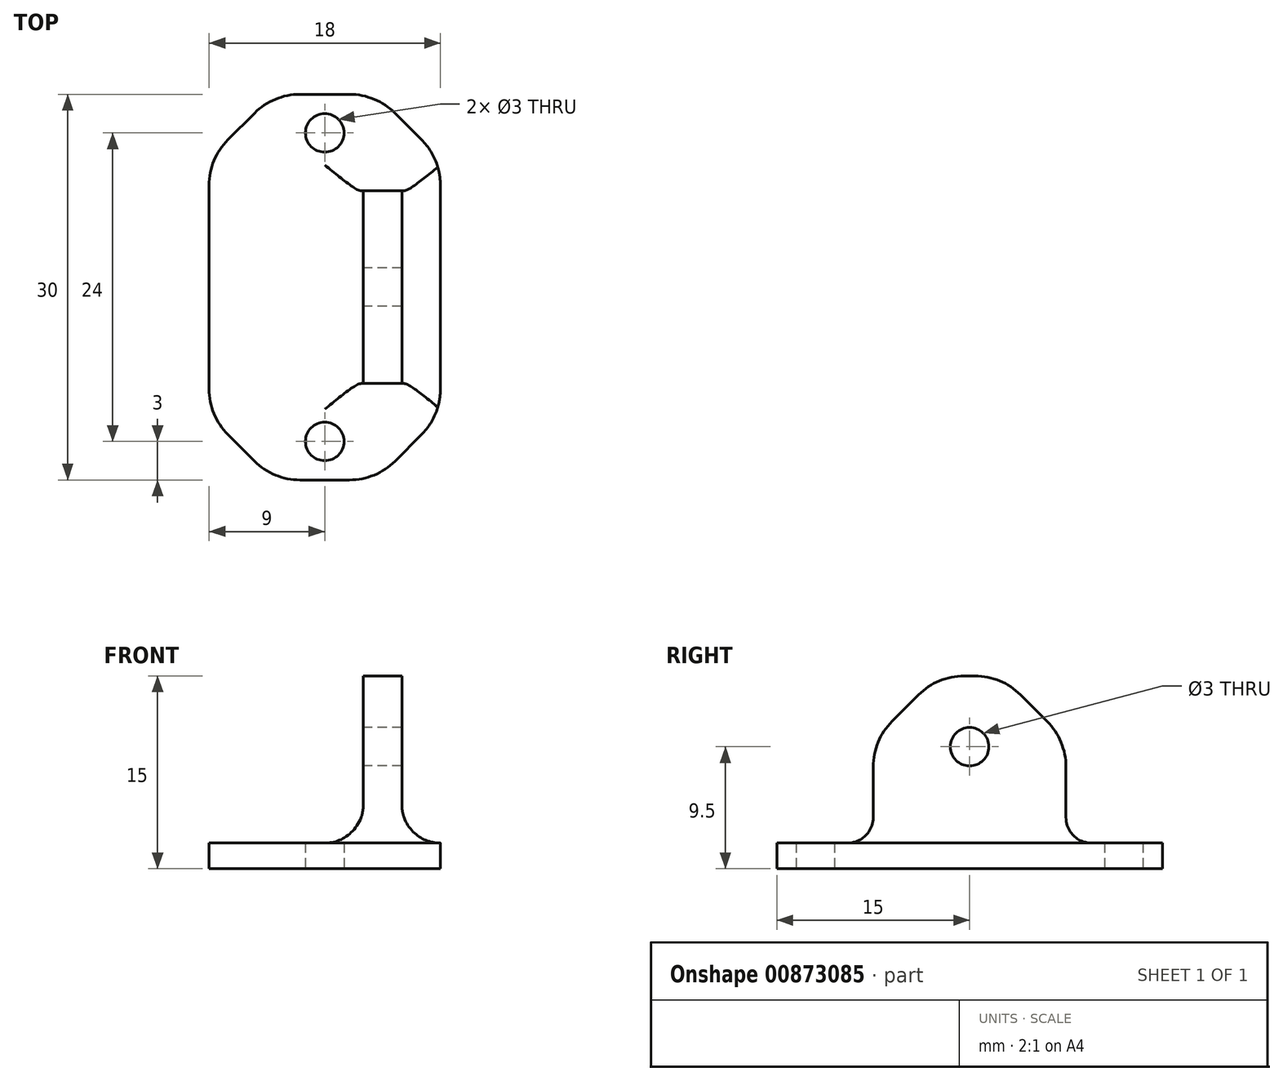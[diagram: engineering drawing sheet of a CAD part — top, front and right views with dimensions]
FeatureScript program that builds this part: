
annotation { "Feature Type Name" : "Feature", "Feature Type Description" : "" }
export const myFeature = defineFeature(function(context is Context, id is Id, definition is map)
    precondition{}
    {
        {
            var Q0;
            Q0=qCreatedBy(makeId("Top.planeOp"),FACE);
            var sketch = newSketch(context, id + "F0", { "sketchPlane" : qUnion([Q0])});
            skLineSegment(sketch, "E0.bottom", {"start": v(9, -15) * mm, "end": v(-9, -15) * mm});
            skLineSegment(sketch, "E0.top", {"start": v(9, 15) * mm, "end": v(-9, 15) * mm});
            skLineSegment(sketch, "E0.left", {"start": v(9, -15) * mm, "end": v(9, 15) * mm});
            skLineSegment(sketch, "E0.right", {"start": v(-9, -15) * mm, "end": v(-9, 15) * mm});
            skPoint(sketch, "E0.middle", {"position": v(0, 0) * mm});
            skLineSegment(sketch, "E1.bottom", {"start": v(6, -7.5) * mm, "end": v(3, -7.5) * mm});
            skLineSegment(sketch, "E1.top", {"start": v(6, 7.5) * mm, "end": v(3, 7.5) * mm});
            skLineSegment(sketch, "E1.left", {"start": v(6, -7.5) * mm, "end": v(6, 7.5) * mm});
            skLineSegment(sketch, "E1.right", {"start": v(3, -7.5) * mm, "end": v(3, 7.5) * mm});
            skPoint(sketch, "E1.middle", {"position": v(4.5, 0) * mm});
            skLineSegment(sketch, "E2", {"start": v(0, 0) * mm, "end": v(3, 0) * mm});
            skLineSegment(sketch, "E3", {"start": v(4.5, -7.5) * mm, "end": v(4.5, -15) * mm, "construction": true});
            skLineSegment(sketch, "E4", {"start": v(0, 0) * mm, "end": v(0, 12) * mm, "construction": true});
            skLineSegment(sketch, "E5", {"start": v(0, 0) * mm, "end": v(0, -12) * mm, "construction": true});
            skCircle(sketch, "E6", {"center": v(0, 12) * mm, "radius": 1.5 * mm});
            skCircle(sketch, "E7", {"center": v(0, -12) * mm, "radius": 1.5 * mm});
            skSolve(sketch);
        }
        {
            var Q0;
            Q0=makeQuery(id+"F0.imprint","IMPRINT",FACE,{"disambiguationData":[TD([[makeQuery(id+"F0.imprint","IMPRINT",EDGE,{"derivedFrom":sQuery(id+"F0.wireOp",EDGE,"E0.bottom")}),-1.0]])]});
            var Q1;
            {var subQ1=sQuery(id+"F0.wireOp",EDGE,"E1.bottom");Q1=makeQuery(id+"F0.imprint","IMPRINT",FACE,{"disambiguationData":[TD([[makeQuery(id+"F0.imprint","IMPRINT",EDGE,{"derivedFrom":subQ1}),-1.0]])]});}
            extrude(context, id + "F1", {"entities" : qUnion([Q0, Q1]), "depth" : 2 * mm, "offsetDistance" : 25 * mm});
        }
        {
            var Q0;
            {var subQ1=sQuery(id+"F0.wireOp",EDGE,"E1.bottom");Q0=makeQuery(id+"F0.imprint","IMPRINT",FACE,{"disambiguationData":[TD([[makeQuery(id+"F0.imprint","IMPRINT",EDGE,{"derivedFrom":subQ1}),-1.0]])]});}
            extrude(context, id + "F2", {"entities" : qUnion([Q0]), "operationType" : NewBodyOperationType.ADD, "depth" : 15 * mm, "offsetDistance" : 25 * mm});
        }
        {
            var Q0;
            Q0=makeQuery(id+"F2.opExtrude","SWEPT_FACE",FACE,{"disambiguationData":[OSD([sQuery(id+"F0.wireOp",EDGE,"E1.right")])]});
            var sketch = newSketch(context, id + "F3", { "sketchPlane" : qUnion([Q0])});
            skCircle(sketch, "E8", {"center": v(0, 9.5) * mm, "radius": 1.5 * mm});
            skPoint(sketch, "E8.centerSnap0", {"position": v(0, 15) * mm});
            skLineSegment(sketch, "E9", {"start": v(0, 15) * mm, "end": v(0, 9.5) * mm, "construction": true});
            skSolve(sketch);
        }
        {
            var Q0;
            Q0=makeQuery(id+"F3.imprint","IMPRINT",FACE,{"disambiguationData":[TD([[makeQuery(id+"F3.imprint","IMPRINT",EDGE,{"derivedFrom":sQuery(id+"F3.wireOp",EDGE,"E8")}),1.0]])]});
            extrude(context, id + "F4", {"entities" : qUnion([Q0]), "operationType" : NewBodyOperationType.REMOVE, "oppositeDirection" : true, "depth" : 25 * mm, "offsetDistance" : 25 * mm});
        }
        {
            var Q0;
            Q0=makeQuery(id+"F2.opExtrude","CAP_EDGE",EDGE,{"disambiguationData":[OSD([sQuery(id+"F0.wireOp",EDGE,"E1.bottom")])],"isStart":false});
            var Q1;
            Q1=makeQuery(id+"F2.opExtrude","CAP_EDGE",EDGE,{"disambiguationData":[OSD([sQuery(id+"F0.wireOp",EDGE,"E1.top")])],"isStart":false});
            chamfer(context, id + "F5", {"entities" : qUnion([Q0, Q1]), "width" : 5 * mm, "tangentPropagation" : true});
        }
        {
            var Q0;
            {var subQ0=sQuery(id+"F0.wireOp",EDGE,"E1.bottom");Q0=makeQuery(id+"F5.opChamfer","BLEND_EDGE",EDGE,{"blendedFrom":[makeQuery(id+"F2.opExtrude","CAP_EDGE",EDGE,{"disambiguationData":[OSD([subQ0])],"isStart":false}),makeQuery(id+"F2.opExtrude","SWEPT_FACE",FACE,{"disambiguationData":[OSD([subQ0])]})],"blendedInto":[makeQuery(id+"F2.opExtrude","SWEPT_FACE",FACE,{"disambiguationData":[OSD([subQ0])]})]});}
            var Q1;
            {var subQ0=sQuery(id+"F0.wireOp",EDGE,"E1.bottom");Q1=makeQuery(id+"F5.opChamfer","BLEND_EDGE",EDGE,{"blendedFrom":[makeQuery(id+"F2.opExtrude","CAP_EDGE",EDGE,{"disambiguationData":[OSD([subQ0])],"isStart":false}),makeQuery(id+"F2.opExtrude","CAP_FACE",FACE,{"disambiguationData":[OSD([subQ0,sQuery(id+"F0.wireOp",EDGE,"E1.top"),sQuery(id+"F0.wireOp",EDGE,"E1.left"),sQuery(id+"F0.wireOp",EDGE,"E1.right")])],"isStart":false})],"blendedInto":[makeQuery(id+"F2.opExtrude","CAP_FACE",FACE,{"disambiguationData":[OSD([subQ0,sQuery(id+"F0.wireOp",EDGE,"E1.top"),sQuery(id+"F0.wireOp",EDGE,"E1.left"),sQuery(id+"F0.wireOp",EDGE,"E1.right")])],"isStart":false})]});}
            var Q2;
            {var subQ0=sQuery(id+"F0.wireOp",EDGE,"E1.top");Q2=makeQuery(id+"F5.opChamfer","BLEND_EDGE",EDGE,{"blendedFrom":[makeQuery(id+"F2.opExtrude","CAP_EDGE",EDGE,{"disambiguationData":[OSD([subQ0])],"isStart":false}),makeQuery(id+"F2.opExtrude","SWEPT_FACE",FACE,{"disambiguationData":[OSD([subQ0])]})],"blendedInto":[makeQuery(id+"F2.opExtrude","SWEPT_FACE",FACE,{"disambiguationData":[OSD([subQ0])]})]});}
            var Q3;
            {var subQ0=sQuery(id+"F0.wireOp",EDGE,"E1.top");Q3=makeQuery(id+"F5.opChamfer","BLEND_EDGE",EDGE,{"blendedFrom":[makeQuery(id+"F2.opExtrude","CAP_EDGE",EDGE,{"disambiguationData":[OSD([subQ0])],"isStart":false}),makeQuery(id+"F2.opExtrude","CAP_FACE",FACE,{"disambiguationData":[OSD([sQuery(id+"F0.wireOp",EDGE,"E1.bottom"),subQ0,sQuery(id+"F0.wireOp",EDGE,"E1.left"),sQuery(id+"F0.wireOp",EDGE,"E1.right")])],"isStart":false})],"blendedInto":[makeQuery(id+"F2.opExtrude","CAP_FACE",FACE,{"disambiguationData":[OSD([sQuery(id+"F0.wireOp",EDGE,"E1.bottom"),subQ0,sQuery(id+"F0.wireOp",EDGE,"E1.left"),sQuery(id+"F0.wireOp",EDGE,"E1.right")])],"isStart":false})]});}
            fillet(context, id + "F6", {"entities" : qUnion([Q0, Q1, Q2, Q3]), "radius" : 5 * mm, "tangentPropagation" : true, "allowEdgeOverflow" : false});
        }
        {
            var Q0;
            Q0=makeQuery(id+"F2.boolean.opBoolean","INTERSECT",EDGE,{"derivedFrom":[makeQuery(id+"F1.opExtrude","CAP_FACE",FACE,{"disambiguationData":[OSD([sQuery(id+"F0.wireOp",EDGE,"E0.bottom"),sQuery(id+"F0.wireOp",EDGE,"E0.top"),sQuery(id+"F0.wireOp",EDGE,"E0.left"),sQuery(id+"F0.wireOp",EDGE,"E0.right"),sQuery(id+"F0.wireOp",EDGE,"E6")])],"isStart":false}),makeQuery(id+"F2.opExtrude","SWEPT_FACE",FACE,{"disambiguationData":[OSD([sQuery(id+"F0.wireOp",EDGE,"E1.left")])]})]});
            var Q1;
            Q1=makeQuery(id+"F2.boolean.opBoolean","INTERSECT",EDGE,{"derivedFrom":[makeQuery(id+"F1.opExtrude","CAP_FACE",FACE,{"disambiguationData":[OSD([sQuery(id+"F0.wireOp",EDGE,"E0.bottom"),sQuery(id+"F0.wireOp",EDGE,"E0.top"),sQuery(id+"F0.wireOp",EDGE,"E0.left"),sQuery(id+"F0.wireOp",EDGE,"E0.right"),sQuery(id+"F0.wireOp",EDGE,"E6")])],"isStart":false}),makeQuery(id+"F2.opExtrude","SWEPT_FACE",FACE,{"disambiguationData":[OSD([sQuery(id+"F0.wireOp",EDGE,"E1.right")])]})]});
            fillet(context, id + "F7", {"entities" : qUnion([Q0, Q1]), "radius" : 3 * mm, "tangentPropagation" : true, "allowEdgeOverflow" : false});
        }
        {
            var Q0;
            Q0=makeQuery(id+"F1.opExtrude","SWEPT_EDGE",EDGE,{"disambiguationData":[OSD([sQuery(id+"F0.wireOp",EDGE,"E0.bottom"),sQuery(id+"F0.wireOp",EDGE,"E0.right")])]});
            var Q1;
            Q1=makeQuery(id+"F1.opExtrude","SWEPT_EDGE",EDGE,{"disambiguationData":[OSD([sQuery(id+"F0.wireOp",EDGE,"E0.bottom"),sQuery(id+"F0.wireOp",EDGE,"E0.left")])]});
            var Q2;
            Q2=makeQuery(id+"F1.opExtrude","SWEPT_EDGE",EDGE,{"disambiguationData":[OSD([sQuery(id+"F0.wireOp",EDGE,"E0.top"),sQuery(id+"F0.wireOp",EDGE,"E0.left")])]});
            var Q3;
            Q3=makeQuery(id+"F1.opExtrude","SWEPT_EDGE",EDGE,{"disambiguationData":[OSD([sQuery(id+"F0.wireOp",EDGE,"E0.top"),sQuery(id+"F0.wireOp",EDGE,"E0.right")])]});
            chamfer(context, id + "F8", {"entities" : qUnion([Q0, Q1, Q2, Q3]), "width" : 5 * mm, "tangentPropagation" : true});
        }
        {
            var Q0;
            {var subQ0=sQuery(id+"F0.wireOp",EDGE,"E0.right");Q0=makeQuery(id+"F8.opChamfer","BLEND_EDGE",EDGE,{"blendedFrom":[makeQuery(id+"F1.opExtrude","SWEPT_EDGE",EDGE,{"disambiguationData":[OSD([sQuery(id+"F0.wireOp",EDGE,"E0.top"),subQ0])]}),makeQuery(id+"F1.opExtrude","SWEPT_FACE",FACE,{"disambiguationData":[OSD([subQ0])]})],"blendedInto":[makeQuery(id+"F1.opExtrude","SWEPT_FACE",FACE,{"disambiguationData":[OSD([subQ0])]})]});}
            var Q1;
            {var subQ0=sQuery(id+"F0.wireOp",EDGE,"E0.top");Q1=makeQuery(id+"F8.opChamfer","BLEND_EDGE",EDGE,{"blendedFrom":[makeQuery(id+"F1.opExtrude","SWEPT_EDGE",EDGE,{"disambiguationData":[OSD([subQ0,sQuery(id+"F0.wireOp",EDGE,"E0.right")])]}),makeQuery(id+"F1.opExtrude","SWEPT_FACE",FACE,{"disambiguationData":[OSD([subQ0])]})],"blendedInto":[makeQuery(id+"F1.opExtrude","SWEPT_FACE",FACE,{"disambiguationData":[OSD([subQ0])]})]});}
            var Q2;
            {var subQ0=sQuery(id+"F0.wireOp",EDGE,"E0.top");Q2=makeQuery(id+"F8.opChamfer","BLEND_EDGE",EDGE,{"blendedFrom":[makeQuery(id+"F1.opExtrude","SWEPT_EDGE",EDGE,{"disambiguationData":[OSD([subQ0,sQuery(id+"F0.wireOp",EDGE,"E0.left")])]}),makeQuery(id+"F1.opExtrude","SWEPT_FACE",FACE,{"disambiguationData":[OSD([subQ0])]})],"blendedInto":[makeQuery(id+"F1.opExtrude","SWEPT_FACE",FACE,{"disambiguationData":[OSD([subQ0])]})]});}
            var Q3;
            {var subQ0=sQuery(id+"F0.wireOp",EDGE,"E0.left");Q3=makeQuery(id+"F8.opChamfer","BLEND_EDGE",EDGE,{"blendedFrom":[makeQuery(id+"F1.opExtrude","SWEPT_EDGE",EDGE,{"disambiguationData":[OSD([sQuery(id+"F0.wireOp",EDGE,"E0.top"),subQ0])]}),makeQuery(id+"F1.opExtrude","SWEPT_FACE",FACE,{"disambiguationData":[OSD([subQ0])]})],"blendedInto":[makeQuery(id+"F1.opExtrude","SWEPT_FACE",FACE,{"disambiguationData":[OSD([subQ0])]})]});}
            var Q4;
            {var subQ0=sQuery(id+"F0.wireOp",EDGE,"E0.right");Q4=makeQuery(id+"F8.opChamfer","BLEND_EDGE",EDGE,{"blendedFrom":[makeQuery(id+"F1.opExtrude","SWEPT_EDGE",EDGE,{"disambiguationData":[OSD([sQuery(id+"F0.wireOp",EDGE,"E0.bottom"),subQ0])]}),makeQuery(id+"F1.opExtrude","SWEPT_FACE",FACE,{"disambiguationData":[OSD([subQ0])]})],"blendedInto":[makeQuery(id+"F1.opExtrude","SWEPT_FACE",FACE,{"disambiguationData":[OSD([subQ0])]})]});}
            var Q5;
            {var subQ0=sQuery(id+"F0.wireOp",EDGE,"E0.bottom");Q5=makeQuery(id+"F8.opChamfer","BLEND_EDGE",EDGE,{"blendedFrom":[makeQuery(id+"F1.opExtrude","SWEPT_EDGE",EDGE,{"disambiguationData":[OSD([subQ0,sQuery(id+"F0.wireOp",EDGE,"E0.right")])]}),makeQuery(id+"F1.opExtrude","SWEPT_FACE",FACE,{"disambiguationData":[OSD([subQ0])]})],"blendedInto":[makeQuery(id+"F1.opExtrude","SWEPT_FACE",FACE,{"disambiguationData":[OSD([subQ0])]})]});}
            var Q6;
            {var subQ0=sQuery(id+"F0.wireOp",EDGE,"E0.bottom");Q6=makeQuery(id+"F8.opChamfer","BLEND_EDGE",EDGE,{"blendedFrom":[makeQuery(id+"F1.opExtrude","SWEPT_EDGE",EDGE,{"disambiguationData":[OSD([subQ0,sQuery(id+"F0.wireOp",EDGE,"E0.left")])]}),makeQuery(id+"F1.opExtrude","SWEPT_FACE",FACE,{"disambiguationData":[OSD([subQ0])]})],"blendedInto":[makeQuery(id+"F1.opExtrude","SWEPT_FACE",FACE,{"disambiguationData":[OSD([subQ0])]})]});}
            var Q7;
            {var subQ0=sQuery(id+"F0.wireOp",EDGE,"E0.left");Q7=makeQuery(id+"F8.opChamfer","BLEND_EDGE",EDGE,{"blendedFrom":[makeQuery(id+"F1.opExtrude","SWEPT_EDGE",EDGE,{"disambiguationData":[OSD([sQuery(id+"F0.wireOp",EDGE,"E0.bottom"),subQ0])]}),makeQuery(id+"F1.opExtrude","SWEPT_FACE",FACE,{"disambiguationData":[OSD([subQ0])]})],"blendedInto":[makeQuery(id+"F1.opExtrude","SWEPT_FACE",FACE,{"disambiguationData":[OSD([subQ0])]})]});}
            fillet(context, id + "F9", {"entities" : qUnion([Q0, Q1, Q2, Q3, Q4, Q5, Q6, Q7]), "radius" : 5 * mm, "tangentPropagation" : true, "allowEdgeOverflow" : false});
        }
        {
            var Q0;
            Q0=makeQuery(id+"F2.boolean.opBoolean","INTERSECT",EDGE,{"derivedFrom":[makeQuery(id+"F1.opExtrude","CAP_FACE",FACE,{"disambiguationData":[OSD([sQuery(id+"F0.wireOp",EDGE,"E0.bottom"),sQuery(id+"F0.wireOp",EDGE,"E0.top"),sQuery(id+"F0.wireOp",EDGE,"E0.left"),sQuery(id+"F0.wireOp",EDGE,"E0.right"),sQuery(id+"F0.wireOp",EDGE,"E6")])],"isStart":false}),makeQuery(id+"F2.opExtrude","SWEPT_FACE",FACE,{"disambiguationData":[OSD([sQuery(id+"F0.wireOp",EDGE,"E1.top")])]})]});
            var Q1;
            Q1=makeQuery(id+"F2.boolean.opBoolean","INTERSECT",EDGE,{"derivedFrom":[makeQuery(id+"F1.opExtrude","CAP_FACE",FACE,{"disambiguationData":[OSD([sQuery(id+"F0.wireOp",EDGE,"E0.bottom"),sQuery(id+"F0.wireOp",EDGE,"E0.top"),sQuery(id+"F0.wireOp",EDGE,"E0.left"),sQuery(id+"F0.wireOp",EDGE,"E0.right"),sQuery(id+"F0.wireOp",EDGE,"E6")])],"isStart":false}),makeQuery(id+"F2.opExtrude","SWEPT_FACE",FACE,{"disambiguationData":[OSD([sQuery(id+"F0.wireOp",EDGE,"E1.bottom")])]})]});
            fillet(context, id + "F10", {"entities" : qUnion([Q0, Q1]), "radius" : 2 * mm, "tangentPropagation" : true, "allowEdgeOverflow" : false});
        }
    });
